# Revit family: Hutprofil 45-45 seitl. Lo
name_source: partatom
category: HLS-Bauteile
units: mm (PartAtom-declared; Revit-internal decimal feet)

## family parameters
Arbeitsebenenbasiert = Ja
Beim Laden mit Abzugskörper schneiden = Nein
Bemaßung runder Anschluss = Durchmesser verwenden
Beschriftungsausrichtung beibehalten = Nein
Gemeinsam genutzt = Ja
Immer vertikal = Nein
Raumberechnungspunkt = Nein
Teiletyp = Normal

## types (1)
- Hutprofil  45
    Anschlusslochung = 13 mm
    Artikelnummer = 08162445
    Breite Material = 35 mm
    EAN = 4250928447975
    Fabrikat = MEFA
    Firma = MEFA Befestigungs- und Montagesysteme GmbH
    Gewicht = 0.21 kg
    Gewicht pro Bauteil = 0.21 kg
    H = 45 mm  [stored 0.147638 ft]
    Höhe = 45 mm
    Kurztext1 = Hutprofil C-Profil 45/45
    Kurztext2 = Höhe 45 mm Langloch 17,5x13 mm
    Langloch = 13 x 17,5 mm
    Lochabstand = 98 mm
    Lochung seitlich = Ja
    Länge = 130 mm  [stored 0.426509 ft]
    Länge Innen = 45 mm
    Material = Stahl
    Materialname = S235
    Mengeneinheit = St
    Oberflaeche = galvanisch verzinkt
    Profiltyp = 45/45
    Stärke Material = 4 mm  [stored 0.0131234 ft]
    Vorgabe-Ansicht = 1219 mm
    max. zul. Last = 3.50 kN
    vpe = 25

note: [stored X ft] marks values corroborated as IEEE doubles in the binary element streams (Revit-internal decimal feet)
